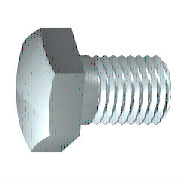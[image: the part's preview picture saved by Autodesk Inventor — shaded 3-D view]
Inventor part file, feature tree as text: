
AUTODESK INVENTOR PART (.ipt)
format: ipt  version: 2023.1 (Build 271208000, 208)  size: 192,512 bytes
history: native  units: mm (DEFAULTED — no unit token found)
features: sketch x3, extrude x1, chamfer x1, plane x1
ambient origin geometry x7: Origin, YZ Plane, XZ Plane, X Axis, Y Axis, Z Axis, Center Point
bodies: Solid1 (feature_tree), Body (feature_tree)
feature tree (6):
  extrude  "Head"  Depth=38.0mm
  chamfer  "Chamfer1"  Distance=9.2mm
  plane  "Work Plane1"
  sketch  "Sketch1"  dims[d0=100.0mm d1=38.0mm]
  sketch  "Sketch2"  dims[d2=16.0mm]
  sketch  "Sketch4"  dims[d12=90.0deg d3=9.2mm d4=0.0mm d5=30.0deg d21=90.0deg d6=0.920175mm d7=0.920275mm d8=0.0mm d9=0.8001mm d10=22.49mm d11=24.0mm d13=0.920275mm d14=16.0mm d15=38.0mm d16=0.0mm d19=24.0mm d55=45.0deg d57=0.0mm d58=0.0mm]
